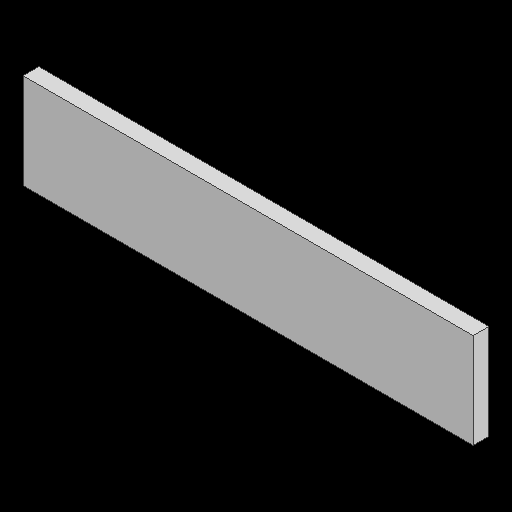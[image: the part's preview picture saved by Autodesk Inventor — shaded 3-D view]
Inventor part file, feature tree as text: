
AUTODESK INVENTOR PART (.ipt)
format: ipt  version: 2025.1 (Build 291241000, 241)  size: 133,120 bytes
history: native  units: in
note: dims shown in document units (in); Inventor stores cm internally (conversion verified against a paired STEP export)
features: other x2, extrude x2, sketch x2, projected_geometry x1
ambient origin geometry x8: Origin, YZ Plane, XZ Plane, XY Plane, X Axis, Y Axis, Z Axis, Center Point
bodies: Body1 (feature_tree)
feature tree (7):
  other  "솔리드1"
  extrude  "돌출1"  Depth=5.5906in
  extrude  "돌출2"  Depth=1.1811in
  sketch  "스케치1"
  other  "스케치 - 직사각형 패턴1"
  sketch  "스케치2"
  projected_geometry  "투영된 루프1"
